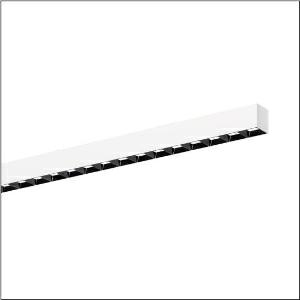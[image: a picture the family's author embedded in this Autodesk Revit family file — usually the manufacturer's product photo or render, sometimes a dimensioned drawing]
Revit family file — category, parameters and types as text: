
# Revit family: silica_r__21_51mx21dc3awb_ae09
name_source: partatom
category: Lighting Fixtures
units: mm (PartAtom-declared; Revit-internal decimal feet)

## family parameters
Cut with Voids When Loaded = No
Host = Face
Light Source = No
Part Type = Normal
Room Calculation Point = No
Round Connector Dimension = Use Diameter
Shared = No

## types (1)
- --- (1 x LED, 10800 lm, 69.3 W, 3000K)
    Apparent Load = 69 VA
    CIE Flux Codes = 87 99 100 100 100
    Color Rendering = 80
    Color Temperature = 3000K
    Default Elevation = 1800 mm
    Description = Silica® 21, office luminaire, primary light control with darklight reflector, of PMMA, black, CAT 2 (L<= 3000cd/m²), light emission: direct distribution, primary light characteristic: symmetric, installation type: surface-mounted, LED, rated luminous flux: 10.800lm, luminous efficacy: 156lm/W, light colour: 830, colour temperature: 3000K, with terminal, 3+2-pole, max. 2.5mm², mains connection: 220..240V, AC, 50/60Hz, luminaire housing, of aluminium, traffic white (RAL 9016), length: 3.004mm, width: 53mm, height: 53mm, protection rating (complete): IP20, insulation class (complete): insulation class I (protective earthing), certification: CE, permissible operating ambient temperature: 0..+35°C, standard: EN 50419, packaging unit: 1 piece
    Height = 0 mm  [stored 0 ft]
    Lamp = 1 x LED
    Lamp Light Flux = 10800 lm
    Lamp Power = 69.3 W
    Lamp count = 1
    Length = 3004 mm
    Luminous efficacy = 156 lm/W
    Manufacturer = Siteco
    ModVariant = No
    Model = 51MX21DC3AWB
    Mounting Place = Ceiling
    Mounting Type = Recessed
    Number of Poles = 1
    OnlyDefault = Yes
    Power Factor = 1
    Product Name = Silica® 21
    Product group = office luminaire | ceiling recessed
    ProductGroupID = 401
    Protection Class = Protection class I
    Protection Degree = IP 20
    RLX_Detail_Level = 1
    RLX_Emergency_Light_Flux = 0 lm
    RLX_Emergency_Type = 0
    RLX_Emergency_Type_DB = No
    RlxData = <blob elided: 61433 chars, md5=430aa1c0>
    Socket = socket
    Standby Power = 0 W
    System Light Flux = 10800 lm
    System Power = 69 W
    Type Comments = factory setting: luminous flux: 100 % | dim-lin: 254 | 393 mA
    Type Image = l_1297779.jpg
    URL = http://relux.com
    VarID = @adj_054779
    Voltage = 0 V
    Weight = 0.00 kg
    Width = 53 mm

note: [stored X ft] marks values corroborated as IEEE doubles in the binary element streams (Revit-internal decimal feet)

## geometry (parser evidence)
native form markers: Blend x4, Sweep x13
no freeform markers — native parametric forms only
